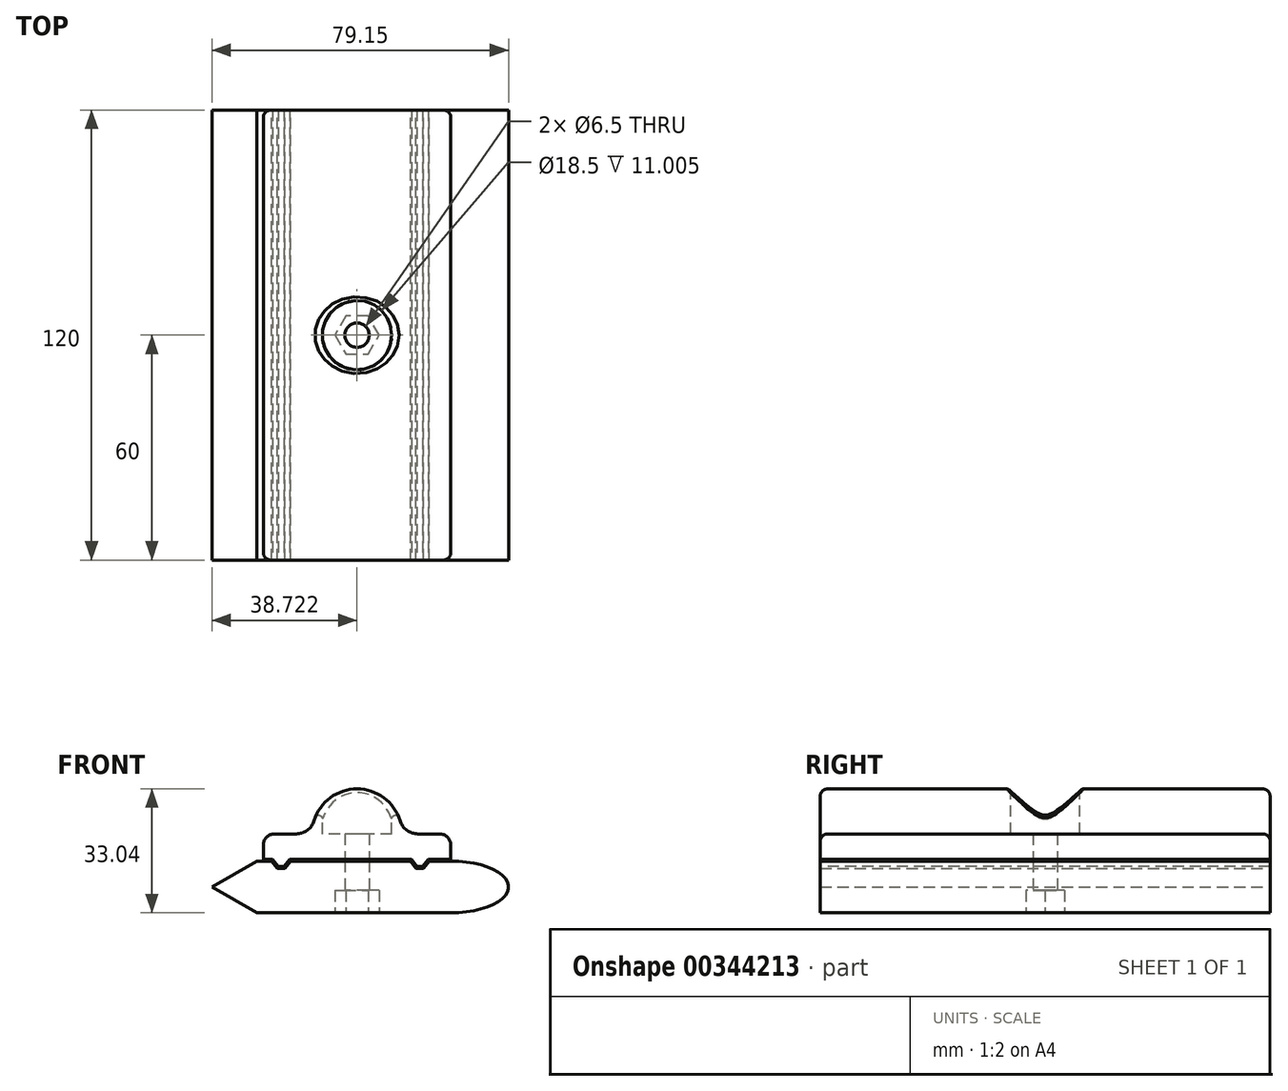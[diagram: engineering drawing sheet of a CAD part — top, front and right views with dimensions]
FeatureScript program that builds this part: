
annotation { "Feature Type Name" : "Feature", "Feature Type Description" : "" }
export const myFeature = defineFeature(function(context is Context, id is Id, definition is map)
    precondition{}
    {
        {
            var Q0;
            Q0=qCreatedBy(makeId("Front.planeOp"),FACE);
            var sketch = newSketch(context, id + "F0", { "sketchPlane" : qUnion([Q0])});
            skLineSegment(sketch, "E0.bottom", {"start": v(30.7, -6.9) * mm, "end": v(-21.02, -6.9) * mm});
            skLineSegment(sketch, "E0.top", {"start": v(28.98, 6.9) * mm, "end": v(24.98, 6.9) * mm});
            skPoint(sketch, "E0.middle", {"position": v(0, 0) * mm});
            skPoint(sketch, "E0.right.end.orphan", {"position": v(-30.7, 6.9) * mm});
            skLineSegment(sketch, "E1", {"start": v(30.7, -6.9) * mm, "end": v(30.7, -6.9) * mm});
            skLineSegment(sketch, "E2", {"start": v(-17.02, 6.9) * mm, "end": v(-15.52, 4.9) * mm});
            skLineSegment(sketch, "E3", {"start": v(-15.52, 4.9) * mm, "end": v(-13.52, 4.9) * mm});
            skLineSegment(sketch, "E4", {"start": v(-13.52, 4.9) * mm, "end": v(-12.02, 6.9) * mm});
            skLineSegment(sketch, "E5.trimOffspring", {"start": v(-17.02, 6.9) * mm, "end": v(-21.02, 6.9) * mm});
            skLineSegment(sketch, "E6", {"start": v(3.98, 6.9) * mm, "end": v(3.98, -0.96) * mm, "construction": true});
            skLineSegment(sketch, "E7.MirrorCS", {"start": v(21.48, 4.9) * mm, "end": v(19.98, 6.9) * mm});
            skLineSegment(sketch, "E8.MirrorCS", {"start": v(23.48, 4.9) * mm, "end": v(21.48, 4.9) * mm});
            skLineSegment(sketch, "E9.MirrorCS", {"start": v(24.98, 6.9) * mm, "end": v(23.48, 4.9) * mm});
            skLineSegment(sketch, "E10.trimOffspring", {"start": v(19.98, 6.9) * mm, "end": v(-12.02, 6.9) * mm});
            skLineSegment(sketch, "E11", {"start": v(-21.02, 6.9) * mm, "end": v(-21.02, -6.9) * mm, "construction": true});
            skLineSegment(sketch, "E12", {"start": v(-21.02, -6.9) * mm, "end": v(30.7, -6.9) * mm, "construction": true});
            skLineSegment(sketch, "E13", {"start": v(30.7, -6.9) * mm, "end": v(30.7, 7.67) * mm, "construction": true});
            skLineSegment(sketch, "E14", {"start": v(28.98, 6.9) * mm, "end": v(30.7, 6.9) * mm});
            skLineSegment(sketch, "E15", {"start": v(-21.02, -6.9) * mm, "end": v(-32.98, 0) * mm});
            skLineSegment(sketch, "E16", {"start": v(-32.98, 0) * mm, "end": v(-21.02, 6.9) * mm});
            skPoint(sketch, "E17.orphan", {"position": v(-28.98, -6.9) * mm});
            skEllipticalArc(sketch, "E18", {});
            const initialGuessF0  = {"E18": [0.030708856271204725, 0, -1, 0, 0.015460294061896578, 0.00690154313497041, 1.5707963267948966, 4.71238898038469]};
            skSetInitialGuess(sketch, initialGuessF0);
            skSolve(sketch);
        }
        {
            var Q0;
            Q0=qSketchRegion(id+"F0",true);
            extrude(context, id + "F1", {"entities" : qUnion([Q0]), "endBound" : BoundingType.SYMMETRIC, "depth" : 120 * mm});
        }
        {
            var Q0;
            Q0=makeQuery(id+"F1.opExtrude","CAP_FACE",FACE,{"disambiguationData":[OSD([sQuery(id+"F0.wireOp",EDGE,"E0.bottom"),sQuery(id+"F0.wireOp",EDGE,"E0.top"),sQuery(id+"F0.wireOp",EDGE,"fYFnA6f6-O799-SNQV-KBHU-91PnJ8zk5QJp"),sQuery(id+"F0.wireOp",EDGE,"8SqoXaY4-CyWe-uXZb-M0PS-nCx8pcjlqL7h"),sQuery(id+"F0.wireOp",EDGE,"E1"),sQuery(id+"F0.wireOp",EDGE,"E2"),sQuery(id+"F0.wireOp",EDGE,"E3"),sQuery(id+"F0.wireOp",EDGE,"E4"),sQuery(id+"F0.wireOp",EDGE,"E5.trimOffspring"),sQuery(id+"F0.wireOp",EDGE,"E7.MirrorCS"),sQuery(id+"F0.wireOp",EDGE,"E8.MirrorCS"),sQuery(id+"F0.wireOp",EDGE,"E9.MirrorCS"),sQuery(id+"F0.wireOp",EDGE,"E10.trimOffspring")])],"isStart":false});
            var sketch = newSketch(context, id + "F2", { "sketchPlane" : qUnion([Q0])});
            skLineSegment(sketch, "E19.0", {"start": v(-16.77, 7.4) * mm, "end": v(-19.26, 7.4) * mm});
            skLineSegment(sketch, "E19.1", {"start": v(-16.77, 7.4) * mm, "end": v(-15.27, 5.4) * mm});
            skLineSegment(sketch, "E19.2", {"start": v(-15.27, 5.4) * mm, "end": v(-13.77, 5.4) * mm});
            skLineSegment(sketch, "E19.3", {"start": v(-13.77, 5.4) * mm, "end": v(-12.27, 7.4) * mm});
            skLineSegment(sketch, "E19.4", {"start": v(20.23, 7.4) * mm, "end": v(-12.27, 7.4) * mm});
            skLineSegment(sketch, "E19.5", {"start": v(30.74, 7.4) * mm, "end": v(24.73, 7.4) * mm});
            skLineSegment(sketch, "E19.6", {"start": v(24.73, 7.4) * mm, "end": v(23.23, 5.4) * mm});
            skLineSegment(sketch, "E19.7", {"start": v(23.23, 5.4) * mm, "end": v(21.73, 5.4) * mm});
            skLineSegment(sketch, "E19.8", {"start": v(21.73, 5.4) * mm, "end": v(20.23, 7.4) * mm});
            skLineSegment(sketch, "E20", {"start": v(-19.26, 7.4) * mm, "end": v(-19.26, 14.14) * mm});
            skLineSegment(sketch, "E21", {"start": v(-19.26, 14.14) * mm, "end": v(-6.26, 14.14) * mm});
            skLineSegment(sketch, "E22", {"start": v(30.74, 14.14) * mm, "end": v(30.74, 7.4) * mm});
            skArc(sketch, "E23", {"start": v(17.74, 14.14) * mm, "mid": v(5.74, 26.14) * mm, "end": v(-6.26, 14.14) * mm});
            skLineSegment(sketch, "E24.trimOffspring", {"start": v(17.74, 14.14) * mm, "end": v(30.74, 14.14) * mm});
            skSolve(sketch);
        }
        {
            var Q0;
            Q0=qSketchRegion(id+"F2",true);
            extrude(context, id + "F3", {"entities" : qUnion([Q0]), "oppositeDirection" : true, "depth" : 120 * mm});
        }
        {
            var Q0;
            Q0=makeQuery(id+"F3.opExtrude","SWEPT_EDGE",EDGE,{"disambiguationData":[OSD([sQuery(id+"F2.wireOp",EDGE,"E23"),sQuery(id+"F2.wireOp",EDGE,"E24.trimOffspring")])]});
            var Q1;
            Q1=makeQuery(id+"F3.opExtrude","SWEPT_EDGE",EDGE,{"disambiguationData":[OSD([sQuery(id+"F2.wireOp",EDGE,"E21"),sQuery(id+"F2.wireOp",EDGE,"E23")])]});
            fillet(context, id + "F4", {"entities" : qUnion([Q0, Q1]), "radius" : 5 * mm, "tangentPropagation" : true, "allowEdgeOverflow" : false});
        }
        {
            var Q0;
            Q0=makeQuery(id+"F3.opExtrude","SWEPT_EDGE",EDGE,{"disambiguationData":[OSD([sQuery(id+"F2.wireOp",EDGE,"E20"),sQuery(id+"F2.wireOp",EDGE,"E21")])]});
            var Q1;
            Q1=makeQuery(id+"F3.opExtrude","SWEPT_EDGE",EDGE,{"disambiguationData":[OSD([sQuery(id+"F2.wireOp",EDGE,"E22"),sQuery(id+"F2.wireOp",EDGE,"E24.trimOffspring")])]});
            fillet(context, id + "F5", {"entities" : qUnion([Q0, Q1]), "radius" : 3 * mm, "tangentPropagation" : true, "allowEdgeOverflow" : false});
        }
        {
            var Q0;
            Q0=qCreatedBy(makeId("Top.planeOp"),FACE);
            var sketch = newSketch(context, id + "F6", { "sketchPlane" : qUnion([Q0])});
            skLineSegment(sketch, "E25", {"start": v(5.74, -58.85) * mm, "end": v(5.74, -28.87) * mm});
            skLineSegment(sketch, "E26", {"start": v(5.74, 57.95) * mm, "end": v(5.74, -28.87) * mm});
            skLineSegment(sketch, "E27", {"start": v(5.74, 57.95) * mm, "end": v(5.74, 58.7) * mm});
            skCircle(sketch, "E28", {"center": v(5.74, 0) * mm, "radius": 3.25 * mm});
            skSolve(sketch);
        }
        {
            var Q0;
            Q0=qSketchRegion(id+"F6",true);
            extrude(context, id + "F7", {"entities" : qUnion([Q0]), "operationType" : NewBodyOperationType.REMOVE, "endBound" : BoundingType.SYMMETRIC, "depth" : 68 * mm});
        }
        {
            var Q0;
            Q0=makeQuery(id+"F1.opExtrude","SWEPT_FACE",FACE,{"disambiguationData":[OSD([sQuery(id+"F0.wireOp",EDGE,"E0.bottom"),sQuery(id+"F0.wireOp",EDGE,"E1")])]});
            var sketch = newSketch(context, id + "F8", { "sketchPlane" : qUnion([Q0])});
            skCircle(sketch, "E29.cCircle", {"center": v(5.74, 0) * mm, "radius": 5.1 * mm, "construction": true});
            skLineSegment(sketch, "E29.0", {"start": v(-0.15, 0) * mm, "end": v(2.8, 5.1) * mm});
            skLineSegment(sketch, "E29.1", {"start": v(2.8, 5.1) * mm, "end": v(8.69, 5.1) * mm});
            skLineSegment(sketch, "E29.2", {"start": v(8.69, 5.1) * mm, "end": v(11.63, 0) * mm});
            skLineSegment(sketch, "E29.3", {"start": v(11.63, 0) * mm, "end": v(8.69, -5.1) * mm});
            skLineSegment(sketch, "E29.4", {"start": v(8.69, -5.1) * mm, "end": v(2.8, -5.1) * mm});
            skLineSegment(sketch, "E29.5", {"start": v(2.8, -5.1) * mm, "end": v(-0.15, 0) * mm});
            skPoint(sketch, "E29.0.midPoint", {"position": v(1.32, 2.55) * mm});
            skSolve(sketch);
        }
        {
            var Q0;
            Q0=qSketchRegion(id+"F8",true);
            extrude(context, id + "F9", {"entities" : qUnion([Q0]), "operationType" : NewBodyOperationType.REMOVE, "oppositeDirection" : true, "depth" : 6 * mm});
        }
        {
            var Q0;
            Q0=sQuery(id+"F2.wireOp",EDGE,"E23");
            cPoint(context, id + "F10", {"entities" : qUnion([Q0]), "parameter" : 0.5});
        }
        {
            var Q0;
            Q0=qCreatedBy(makeId("Top.planeOp"),FACE);
            var Q1;
            Q1=qCreatedBy(id+"F10",VERTEX);
            cPlane(context, id + "F11", {"entities" : qUnion([Q0, Q1]), "cplaneType" : CPlaneType.PLANE_POINT, "offset" : 29.2 * mm, "width" : 150 * mm, "height" : 150 * mm});
        }
        {
            var Q0;
            Q0=qCreatedBy(id+"F11.planeOp",FACE);
            var sketch = newSketch(context, id + "F12", { "sketchPlane" : qUnion([Q0])});
            skCircle(sketch, "E30.0", {"center": v(5.74, 0) * mm, "radius": 9.25 * mm});
            skSolve(sketch);
        }
        {
            var Q0;
            Q0=qSketchRegion(id+"F12",true);
            extrude(context, id + "F13", {"entities" : qUnion([Q0]), "operationType" : NewBodyOperationType.REMOVE, "oppositeDirection" : true, "depth" : 12 * mm});
        }
        {
            var Q0;
            Q0=makeQuery(id+"F13.boolean.opBoolean","INTERSECT",EDGE,{"derivedFrom":[makeQuery(id+"F3.opExtrude","SWEPT_FACE",FACE,{"disambiguationData":[OSD([sQuery(id+"F2.wireOp",EDGE,"E23")])]}),makeQuery(id+"F13.opExtrude","SWEPT_FACE",FACE,{"disambiguationData":[OSD([sQuery(id+"F12.wireOp",EDGE,"E30.0")])]})]});
            fillet(context, id + "F14", {"entities" : qUnion([Q0]), "radius" : 1 * mm, "tangentPropagation" : true, "allowEdgeOverflow" : false});
        }
        {
            var Q0;
            Q0=makeQuery(id+"F3.opExtrude","CAP_EDGE",EDGE,{"disambiguationData":[OSD([sQuery(id+"F2.wireOp",EDGE,"E23")])],"isStart":true});
            var Q1;
            Q1=makeQuery(id+"F3.opExtrude","CAP_EDGE",EDGE,{"disambiguationData":[OSD([sQuery(id+"F2.wireOp",EDGE,"E23")])],"isStart":false});
            fillet(context, id + "F15", {"entities" : qUnion([Q0, Q1]), "radius" : 2 * mm, "tangentPropagation" : true, "allowEdgeOverflow" : false});
        }
    });
